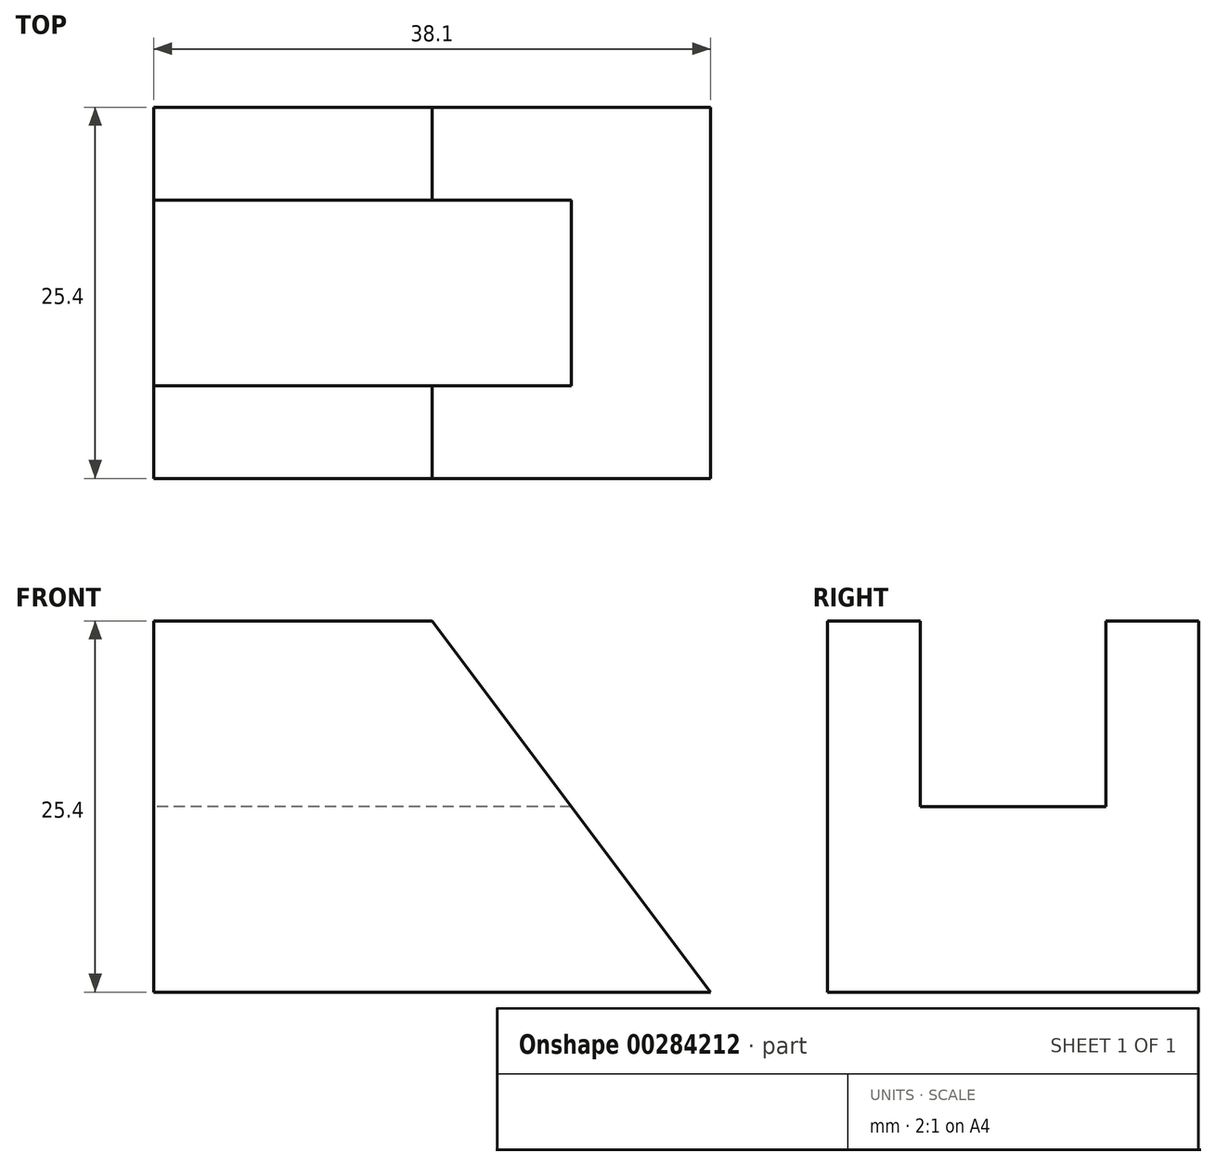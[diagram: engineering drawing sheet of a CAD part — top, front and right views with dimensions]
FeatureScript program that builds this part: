
annotation { "Feature Type Name" : "Feature", "Feature Type Description" : "" }
export const myFeature = defineFeature(function(context is Context, id is Id, definition is map)
    precondition{}
    {
        {
            var Q0;
            Q0=qCreatedBy(makeId("Front.planeOp"),FACE);
            var sketch = newSketch(context, id + "F0", { "sketchPlane" : qUnion([Q0])});
            skLineSegment(sketch, "E0", {"start": v(0, 0) * mm, "end": v(0, 25.4) * mm});
            skLineSegment(sketch, "E1", {"start": v(0, 25.4) * mm, "end": v(19.05, 25.4) * mm});
            skLineSegment(sketch, "E2", {"start": v(19.05, 25.4) * mm, "end": v(38.1, 0) * mm});
            skLineSegment(sketch, "E3", {"start": v(38.1, 0) * mm, "end": v(0, 0) * mm});
            skSolve(sketch);
        }
        {
            var Q0;
            Q0=makeQuery(id+"F0.imprint","IMPRINT",FACE,{"disambiguationData":[TD([[makeQuery(id+"F0.imprint","IMPRINT",EDGE,{"derivedFrom":sQuery(id+"F0.wireOp",EDGE,"E0")}),-1.0]])]});
            extrude(context, id + "F1", {"entities" : qUnion([Q0]), "endBound" : BoundingType.SYMMETRIC, "depth" : 25.4 * mm});
        }
        {
            var Q0;
            Q0=makeQuery(id+"F1.opExtrude","SWEPT_FACE",FACE,{"disambiguationData":[OSD([sQuery(id+"F0.wireOp",EDGE,"E0")])]});
            var sketch = newSketch(context, id + "F2", { "sketchPlane" : qUnion([Q0])});
            skLineSegment(sketch, "E4.bottom", {"start": v(-6.35, 25.4) * mm, "end": v(6.35, 25.4) * mm});
            skLineSegment(sketch, "E4.top", {"start": v(-6.35, 12.7) * mm, "end": v(6.35, 12.7) * mm});
            skLineSegment(sketch, "E4.left", {"start": v(-6.35, 25.4) * mm, "end": v(-6.35, 12.7) * mm});
            skLineSegment(sketch, "E4.right", {"start": v(6.35, 25.4) * mm, "end": v(6.35, 12.7) * mm});
            skSolve(sketch);
        }
        {
            var Q0;
            Q0=makeQuery(id+"F2.imprint","IMPRINT",FACE,{"disambiguationData":[TD([[makeQuery(id+"F2.imprint","IMPRINT",EDGE,{"derivedFrom":sQuery(id+"F2.wireOp",EDGE,"E4.bottom")}),1.0]])]});
            extrude(context, id + "F3", {"entities" : qUnion([Q0]), "operationType" : NewBodyOperationType.REMOVE, "endBound" : BoundingType.THROUGH_ALL, "oppositeDirection" : true, "depth" : 25.4 * mm});
        }
    });
